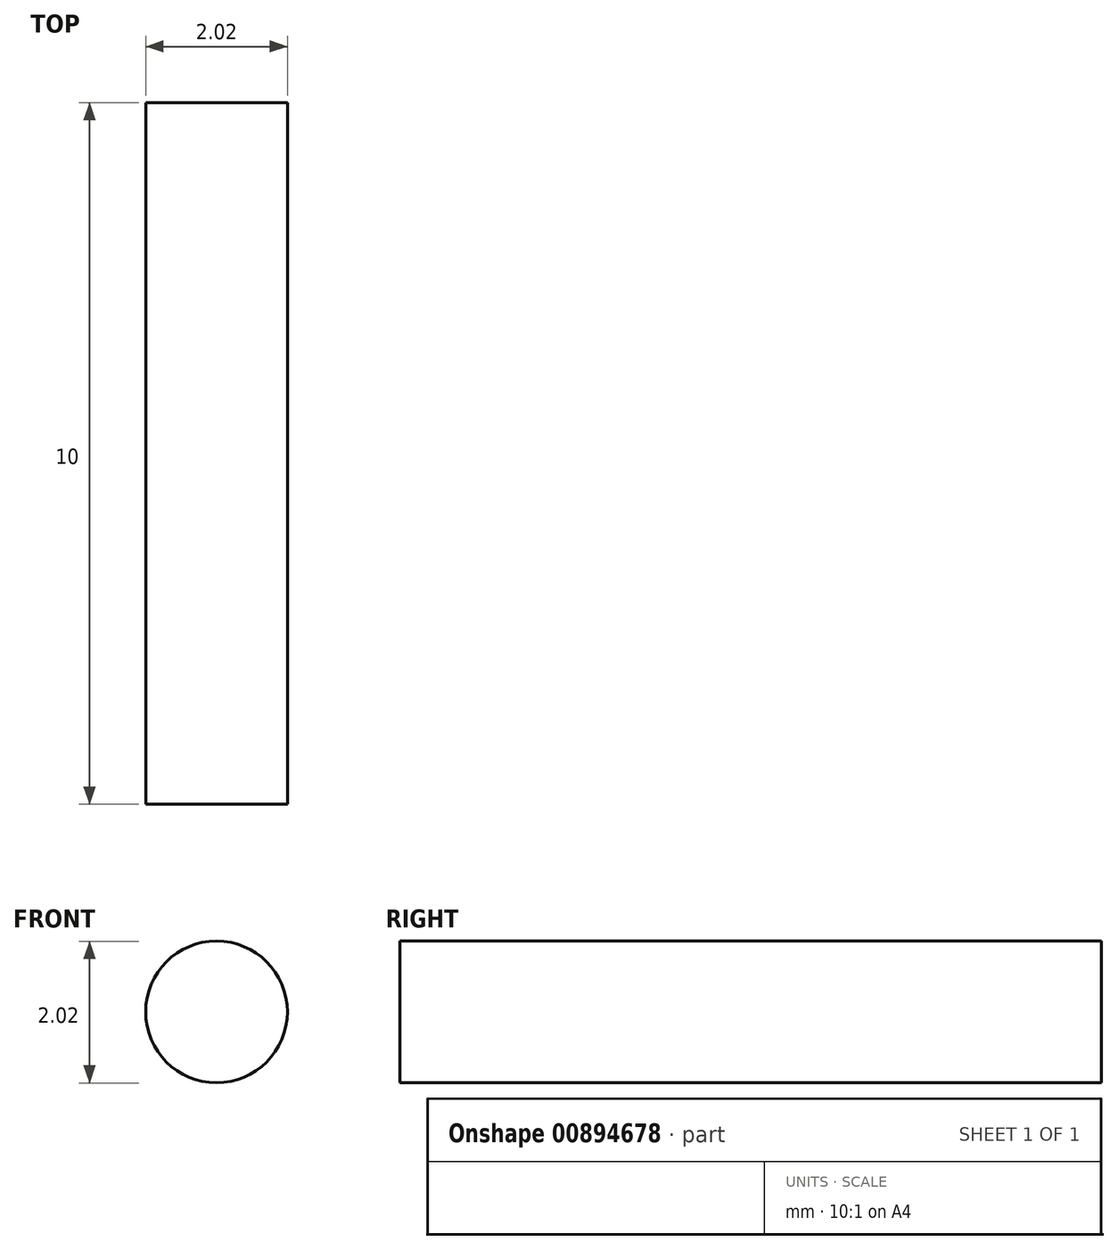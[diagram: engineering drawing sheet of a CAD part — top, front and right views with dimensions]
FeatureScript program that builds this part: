
annotation { "Feature Type Name" : "Feature", "Feature Type Description" : "" }
export const myFeature = defineFeature(function(context is Context, id is Id, definition is map)
    precondition{}
    {
        {
            var Q0;
            Q0=qCreatedBy(makeId("Front.planeOp"),FACE);
            var sketch = newSketch(context, id + "F0", { "sketchPlane" : qUnion([Q0])});
            skCircle(sketch, "E0", {"center": v(-10.3, 24.2) * mm, "radius": 1.01 * mm});
            skSolve(sketch);
        }
        {
            var Q0;
            Q0 = qSketchRegion(id + "F0", true);
            extrude(context, id + "F1", {"entities" : qUnion([Q0]), "oppositeDirection" : true, "depth" : 10 * mm, "offsetDistance" : 25.4 * mm});
        }
        {
            var Q0;
            Q0=qCreatedBy(makeId("Front.planeOp"),FACE);
            var sketch = newSketch(context, id + "F2", { "sketchPlane" : qUnion([Q0])});
            skCircle(sketch, "E1", {"center": v(-138.3, 37.22) * mm, "radius": 1.58 * mm});
            skSolve(sketch);
        }
        {
            var Q0;
            Q0=sQuery(id+"F2.wireOp",EDGE,"E1");
            extrude(context, id + "F3", {"bodyType" : ToolBodyType.SURFACE, "surfaceEntities" : qUnion([Q0]), "depth" : 30 * mm, "offsetDistance" : 25.4 * mm});
        }
    });
